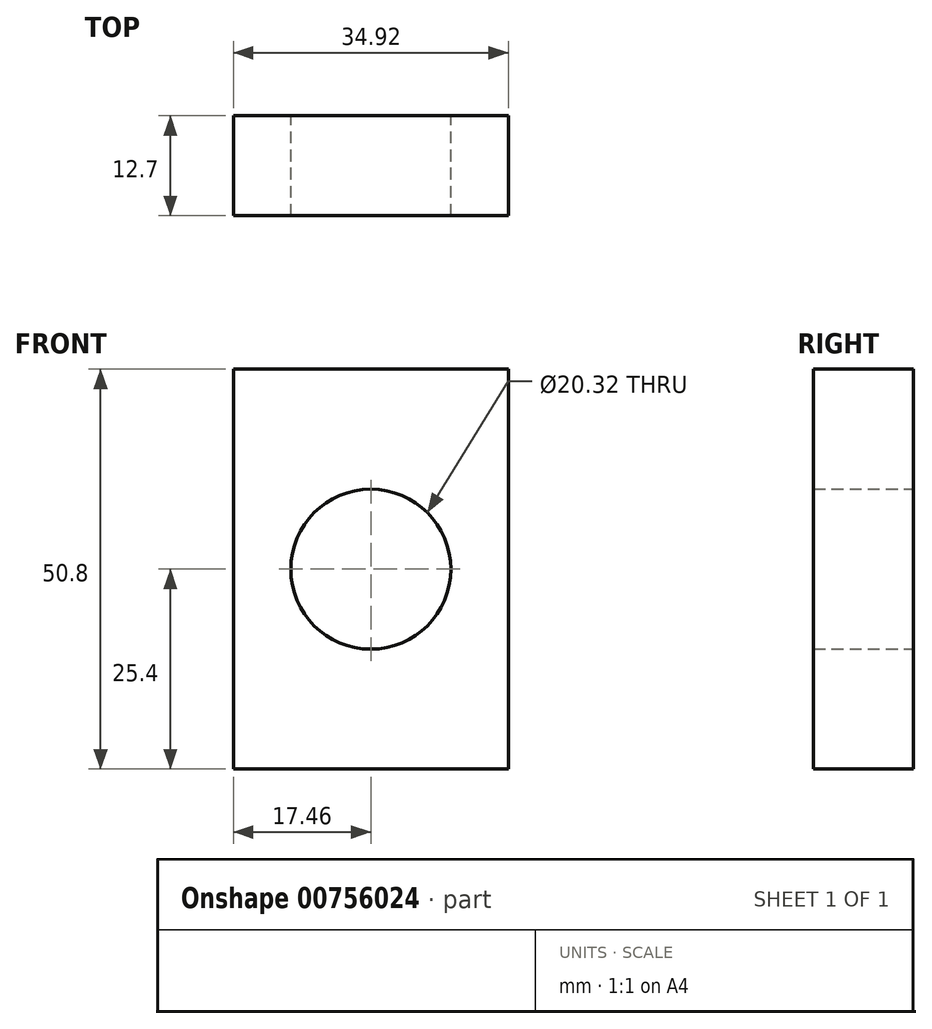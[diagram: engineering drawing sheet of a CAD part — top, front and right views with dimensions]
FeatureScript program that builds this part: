
annotation { "Feature Type Name" : "Feature", "Feature Type Description" : "" }
export const myFeature = defineFeature(function(context is Context, id is Id, definition is map)
    precondition{}
    {
        {
            var Q0;
            Q0=qCreatedBy(makeId("Front.planeOp"),FACE);
            var sketch = newSketch(context, id + "F0", { "sketchPlane" : qUnion([Q0])});
            skLineSegment(sketch, "E0.bottom", {"start": v(-17.46, 25.4) * mm, "end": v(17.46, 25.4) * mm});
            skLineSegment(sketch, "E0.top", {"start": v(-17.46, -25.4) * mm, "end": v(17.46, -25.4) * mm});
            skLineSegment(sketch, "E0.left", {"start": v(-17.46, 25.4) * mm, "end": v(-17.46, -25.4) * mm});
            skLineSegment(sketch, "E0.right", {"start": v(17.46, 25.4) * mm, "end": v(17.46, -25.4) * mm});
            skPoint(sketch, "E0.middle", {"position": v(0, 0) * mm});
            skCircle(sketch, "E1", {"center": v(0, 0) * mm, "radius": 10.16 * mm});
            skSolve(sketch);
        }
        {
            var Q0;
            Q0=makeQuery(id+"F0.imprint","IMPRINT",FACE,{"disambiguationData":[TD([[makeQuery(id+"F0.imprint","IMPRINT",EDGE,{"derivedFrom":sQuery(id+"F0.wireOp",EDGE,"E0.bottom")}),-1.0]])]});
            extrude(context, id + "F1", {"entities" : qUnion([Q0]), "depth" : 12.7 * mm, "offsetDistance" : 25.4 * mm});
        }
    });
